# Revit family: SanitaryComboUnit_Metlam_2-in-1
name_source: partatom
category: Generic Models
revit_build: Autodesk Revit Architecture 2013 (Build: 20120221_2030(x64)
units: mm (PartAtom-declared; Revit-internal decimal feet)

## types (4) — shared parameters
Assembly Code = E1090900
Description = Paper Towel Dispenser & Waste
FilterObject_ANZRS = Sanitary Combination Unit
Height = 1397 mm  [stored 4.58333 ft]
Manufacturer = Metlam
Material = Stainless Steel, Satin
ModifiedIssue_ANZRS = 130318.01 $
StyleOrType_ANZRS = Sanitary Ware
URL = http://www.metlam.com.au
Width = 333 mm  [stored 1.09252 ft]
zero-valued in all types: Default Elevation

## per-type parameters (varying)
| type | Depth | Keywords | Model | Position - Recessed/Suface Mounted | Product Code | Surround | Surround Depth | Void Depth |
| Metlam Sanitary - Paper/Waste 99 Recessed | 115 mm  [stored 0.377297 ft] | DISPENSES 600 C-fold paper towels or 800 Multi-fold paper towels. DISPOSAL 19L removable S.S. waste container. | Paper/Waste - 99 Recessed | 15 mm  [stored 0.0492126 ft] | ML 706 | No | 100 mm  [stored 0.328084 ft] | -108 mm  [stored -0.354331 ft] |
| Metlam Sanitary - Paper/Waste 99 Surface Mounted | 115 mm  [stored 0.377297 ft] | DISPENSES 600 C-fold paper towels or 800 Multi-fold paper towels. DISPOSAL 19L removable S.S. waste container. | Paper/Waste - 99 Surface Mounted | 115 mm  [stored 0.377297 ft] | ML 706 SM | Yes | 100 mm  [stored 0.328084 ft] | -2 mm  [stored -0.00656168 ft] |
| Metlam Sanitary - Paper/Waste 159 Recessed | 155 mm  [stored 0.50853 ft] | DISPENSES 600 C-fold paper towels or 800 Multi-fold paper towels. DISPOSAL 22L removable S.S. waste container. | Paper/Waste - 159 Recessed | 15 mm  [stored 0.0492126 ft] | ML 707 | No | 140 mm  [stored 0.459318 ft] | -160 mm  [stored -0.524934 ft] |
| Metlam Sanitary - Paper/Waste 159 Surface Mounted | 155 mm  [stored 0.50853 ft] | DISPENSES 600 C-fold paper towels or 800 Multi-fold paper towels. DISPOSAL 22L removable S.S. waste container. | Paper/Waste - 159 Surface Mounted | 155 mm  [stored 0.50853 ft] | ML 707 SM | Yes | 140 mm  [stored 0.459318 ft] | -2 mm  [stored -0.00656168 ft] |

note: [stored X ft] marks values corroborated as IEEE doubles in the binary element streams (Revit-internal decimal feet)

## geometry (parser evidence)
native form markers: Blend x28, Extrusion x1, Sweep x1
no freeform markers — native parametric forms only
